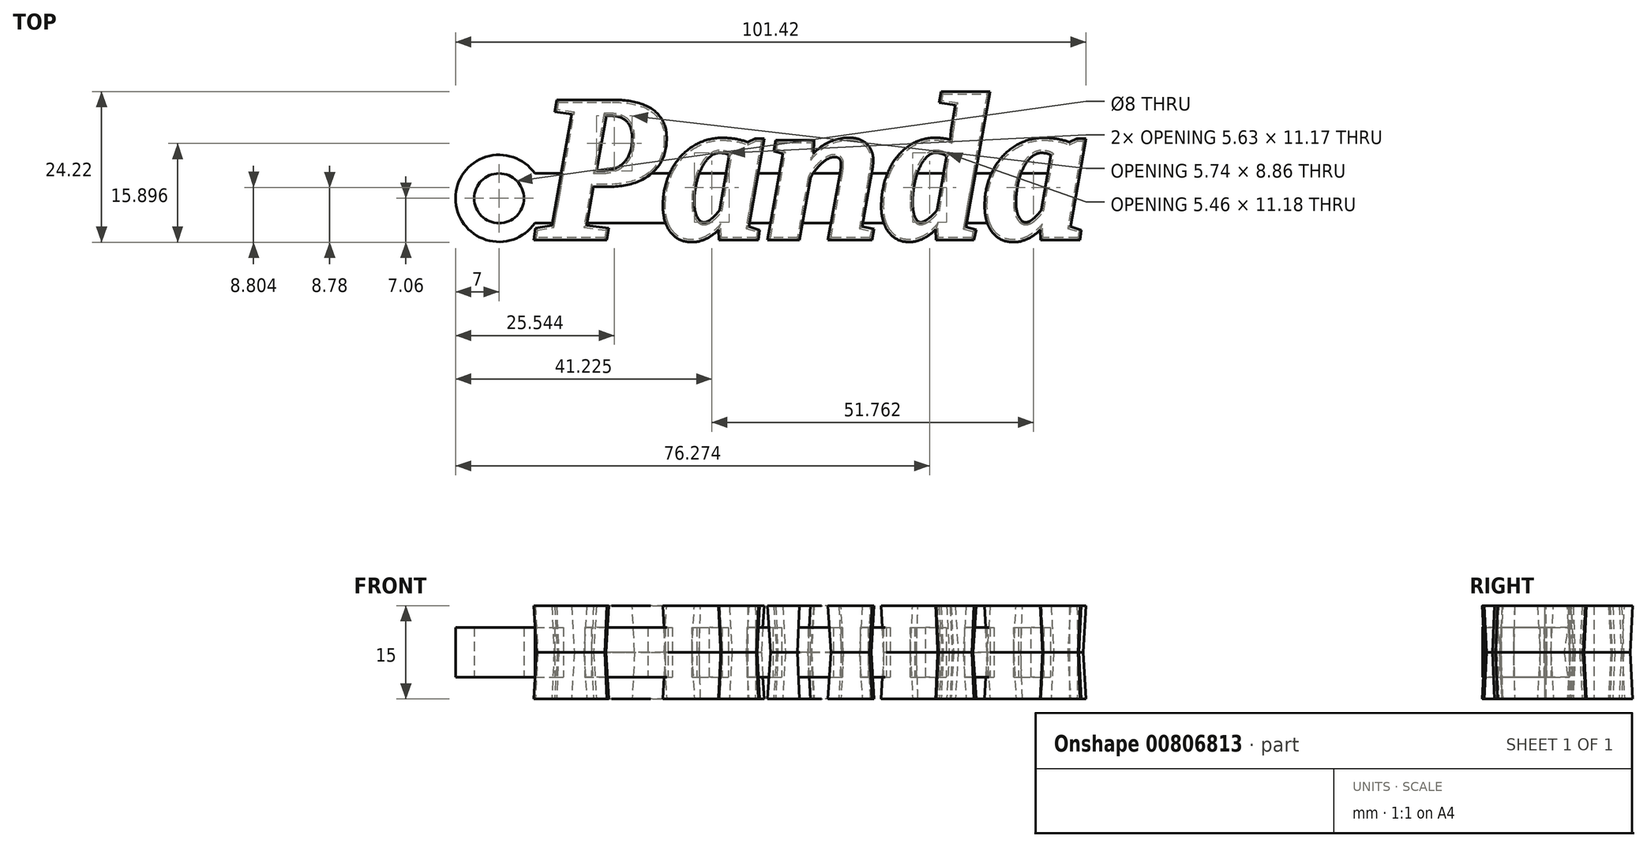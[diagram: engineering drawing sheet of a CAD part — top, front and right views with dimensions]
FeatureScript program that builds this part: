
annotation { "Feature Type Name" : "Feature", "Feature Type Description" : "" }
export const myFeature = defineFeature(function(context is Context, id is Id, definition is map)
    precondition{}
    {
        {
            var Q0;
            Q0=qCreatedBy(makeId("Top.planeOp"),FACE);
            var sketch = newSketch(context, id + "F0", { "sketchPlane" : qUnion([Q0])});
            skLineSegment(sketch, "E0.bottom", {"start": v(-45, 0) * mm, "end": v(45, 0) * mm});
            skLineSegment(sketch, "E0.top", {"start": v(-45, -8) * mm, "end": v(45, -8) * mm});
            skLineSegment(sketch, "E0.left", {"start": v(-45, 0) * mm, "end": v(-45, -8) * mm});
            skLineSegment(sketch, "E0.right", {"start": v(45, 0) * mm, "end": v(45, -8) * mm});
            skCircle(sketch, "E1", {"center": v(-45, -4) * mm, "radius": 7 * mm});
            skCircle(sketch, "E2.0", {"center": v(-45, -4) * mm, "radius": 4 * mm});
            skText(sketch, "E3", { "text": "Panda", "fontName": "Tinos-BoldItalic.ttf"});
            const initialGuessF0  = {"E3": [-0.03896, -0.01032, 1, 0, 0.02395]};
            skSetInitialGuess(sketch, initialGuessF0);
            skSolve(sketch);
        }
        {
            var Q0;
            {var subQ2=sQuery(id+"F0.wireOp",EDGE,"E0.bottom");var subQ4=sQuery(id+"F0.wireOp",EDGE,"E1");var subQ5=makeQuery(id+"F0.imprint","INTERSECT",VERTEX,{"derivedFrom":[subQ2,subQ4]});Q0=makeQuery(id+"F0.imprint","IMPRINT",FACE,{"disambiguationData":[TD([[makeQuery(id+"F0.imprint","IMPRINT",EDGE,{"disambiguationData":[TD([[subQ5,-1.0]])],"derivedFrom":subQ4}),1.0]])]});}
            var Q1;
            {var subQ2=sQuery(id+"F0.wireOp",EDGE,"E0.bottom");var subQ4=sQuery(id+"F0.wireOp",EDGE,"E1");var subQ5=makeQuery(id+"F0.imprint","INTERSECT",VERTEX,{"derivedFrom":[subQ2,subQ4]});Q1=makeQuery(id+"F0.imprint","IMPRINT",FACE,{"disambiguationData":[TD([[makeQuery(id+"F0.imprint","IMPRINT",EDGE,{"disambiguationData":[TD([[subQ5,1.0]])],"derivedFrom":subQ4}),1.0]])]});}
            var Q2;
            {var subQ0=sQuery(id+"F0.wireOp",EDGE,"E1");var subQ1=sQuery(id+"F0.wireOp",EDGE,"E0.bottom");var subQ2=makeQuery(id+"F0.imprint","INTERSECT",VERTEX,{"derivedFrom":[subQ1,subQ0]});Q2=makeQuery(id+"F0.imprint","IMPRINT",FACE,{"disambiguationData":[TD([[makeQuery(id+"F0.imprint","IMPRINT",EDGE,{"disambiguationData":[TD([[subQ2,-1.0]])],"derivedFrom":subQ1}),-1.0]])]});}
            var Q3;
            {var subQ0=sQuery(id+"F0.wireOp",EDGE,"E3.sketch_text.stroke-20");Q3=makeQuery(id+"F0.imprint","IMPRINT",FACE,{"disambiguationData":[TD([[makeQuery(id+"F0.imprint","IMPRINT",EDGE,{"derivedFrom":subQ0}),1.0]])]});}
            var Q4;
            {var subQ5=sQuery(id+"F0.wireOp",EDGE,"E3.sketch_text.stroke-45");Q4=makeQuery(id+"F0.imprint","IMPRINT",FACE,{"disambiguationData":[TD([[makeQuery(id+"F0.imprint","IMPRINT",EDGE,{"derivedFrom":subQ5}),1.0]])]});}
            var Q5;
            {var subQ0=sQuery(id+"F0.wireOp",EDGE,"E3.sketch_text.stroke-36");var subQ1=sQuery(id+"F0.wireOp",EDGE,"E0.bottom");var subQ2=makeQuery(id+"F0.imprint","INTERSECT",VERTEX,{"derivedFrom":[subQ1,subQ0]});Q5=makeQuery(id+"F0.imprint","IMPRINT",FACE,{"disambiguationData":[TD([[makeQuery(id+"F0.imprint","IMPRINT",EDGE,{"disambiguationData":[TD([[subQ2,-1.0]])],"derivedFrom":subQ1}),-1.0]])]});}
            var Q6;
            {var subQ5=sQuery(id+"F0.wireOp",EDGE,"E3.sketch_text.stroke-68");Q6=makeQuery(id+"F0.imprint","IMPRINT",FACE,{"disambiguationData":[TD([[makeQuery(id+"F0.imprint","IMPRINT",EDGE,{"derivedFrom":subQ5}),1.0]])]});}
            var Q7;
            {var subQ5=sQuery(id+"F0.wireOp",EDGE,"E3.sketch_text.stroke-94");Q7=makeQuery(id+"F0.imprint","IMPRINT",FACE,{"disambiguationData":[TD([[makeQuery(id+"F0.imprint","IMPRINT",EDGE,{"derivedFrom":subQ5}),1.0]])]});}
            var Q8;
            {var subQ0=sQuery(id+"F0.wireOp",EDGE,"E3.sketch_text.stroke-103");Q8=makeQuery(id+"F0.imprint","IMPRINT",FACE,{"disambiguationData":[TD([[makeQuery(id+"F0.imprint","IMPRINT",EDGE,{"derivedFrom":subQ0}),1.0]])]});}
            var Q9;
            {var subQ5=sQuery(id+"F0.wireOp",EDGE,"E3.sketch_text.stroke-118");Q9=makeQuery(id+"F0.imprint","IMPRINT",FACE,{"disambiguationData":[TD([[makeQuery(id+"F0.imprint","IMPRINT",EDGE,{"derivedFrom":subQ5}),1.0]])]});}
            var Q10;
            {var subQ1=sQuery(id+"F0.wireOp",EDGE,"E3.sketch_text.stroke-48");var subQ3=sQuery(id+"F0.wireOp",EDGE,"E0.bottom");var subQ4=makeQuery(id+"F0.imprint","INTERSECT",VERTEX,{"derivedFrom":[subQ3,subQ1]});Q10=makeQuery(id+"F0.imprint","IMPRINT",FACE,{"disambiguationData":[TD([[makeQuery(id+"F0.imprint","IMPRINT",EDGE,{"disambiguationData":[TD([[subQ4,-1.0]])],"derivedFrom":subQ3}),-1.0]])]});}
            extrude(context, id + "F1", {"entities" : qUnion([Q0, Q1, Q2, Q3, Q4, Q5, Q6, Q7, Q8, Q9, Q10]), "endBound" : BoundingType.SYMMETRIC, "depth" : 8 * mm, "offsetDistance" : 25 * mm});
        }
        {
            var Q0;
            Q0=makeQuery(id+"F0.imprint","IMPRINT",FACE,{"disambiguationData":[TD([[makeQuery(id+"F0.imprint","IMPRINT",EDGE,{"derivedFrom":sQuery(id+"F0.wireOp",EDGE,"E3.sketch_text.stroke-0")}),-1.0]])]});
            var Q1;
            {var subQ0=sQuery(id+"F0.wireOp",EDGE,"E3.sketch_text.stroke-21");Q1=makeQuery(id+"F0.imprint","IMPRINT",FACE,{"disambiguationData":[TD([[makeQuery(id+"F0.imprint","IMPRINT",EDGE,{"derivedFrom":subQ0}),-1.0]])]});}
            var Q2;
            {var subQ0=sQuery(id+"F0.wireOp",EDGE,"E3.sketch_text.stroke-8");Q2=makeQuery(id+"F0.imprint","IMPRINT",FACE,{"disambiguationData":[TD([[makeQuery(id+"F0.imprint","IMPRINT",EDGE,{"derivedFrom":subQ0}),-1.0]])]});}
            var Q3;
            {var subQ8=sQuery(id+"F0.wireOp",EDGE,"E3.sketch_text.stroke-37");Q3=makeQuery(id+"F0.imprint","IMPRINT",FACE,{"disambiguationData":[TD([[makeQuery(id+"F0.imprint","IMPRINT",EDGE,{"derivedFrom":subQ8}),-1.0]])]});}
            var Q4;
            {var subQ5=sQuery(id+"F0.wireOp",EDGE,"E3.sketch_text.stroke-40");Q4=makeQuery(id+"F0.imprint","IMPRINT",FACE,{"disambiguationData":[TD([[makeQuery(id+"F0.imprint","IMPRINT",EDGE,{"derivedFrom":subQ5}),-1.0]])]});}
            var Q5;
            {var subQ11=sQuery(id+"F0.wireOp",EDGE,"E3.sketch_text.stroke-31");Q5=makeQuery(id+"F0.imprint","IMPRINT",FACE,{"disambiguationData":[TD([[makeQuery(id+"F0.imprint","IMPRINT",EDGE,{"derivedFrom":subQ11}),-1.0]])]});}
            var Q6;
            {var subQ11=sQuery(id+"F0.wireOp",EDGE,"E3.sketch_text.stroke-22");Q6=makeQuery(id+"F0.imprint","IMPRINT",FACE,{"disambiguationData":[TD([[makeQuery(id+"F0.imprint","IMPRINT",EDGE,{"derivedFrom":subQ11}),-1.0]])]});}
            var Q7;
            {var subQ3=sQuery(id+"F0.wireOp",EDGE,"E0.bottom");var subQ5=sQuery(id+"F0.wireOp",EDGE,"E3.sketch_text.stroke-51");var subQ6=makeQuery(id+"F0.imprint","INTERSECT",VERTEX,{"derivedFrom":[subQ3,subQ5]});Q7=makeQuery(id+"F0.imprint","IMPRINT",FACE,{"disambiguationData":[TD([[makeQuery(id+"F0.imprint","IMPRINT",EDGE,{"disambiguationData":[TD([[subQ6,-1.0]])],"derivedFrom":subQ3}),-1.0]])]});}
            var Q8;
            {var subQ11=sQuery(id+"F0.wireOp",EDGE,"E3.sketch_text.stroke-46");Q8=makeQuery(id+"F0.imprint","IMPRINT",FACE,{"disambiguationData":[TD([[makeQuery(id+"F0.imprint","IMPRINT",EDGE,{"derivedFrom":subQ11}),-1.0]])]});}
            var Q9;
            {var subQ1=sQuery(id+"F0.wireOp",EDGE,"E3.sketch_text.stroke-59");var subQ5=sQuery(id+"F0.wireOp",EDGE,"E0.bottom");var subQ6=makeQuery(id+"F0.imprint","INTERSECT",VERTEX,{"derivedFrom":[subQ5,subQ1]});Q9=makeQuery(id+"F0.imprint","IMPRINT",FACE,{"disambiguationData":[TD([[makeQuery(id+"F0.imprint","IMPRINT",EDGE,{"disambiguationData":[TD([[subQ6,1.0]])],"derivedFrom":subQ5}),-1.0]])]});}
            var Q10;
            {var subQ0=sQuery(id+"F0.wireOp",EDGE,"E3.sketch_text.stroke-61");Q10=makeQuery(id+"F0.imprint","IMPRINT",FACE,{"disambiguationData":[TD([[makeQuery(id+"F0.imprint","IMPRINT",EDGE,{"derivedFrom":subQ0}),-1.0]])]});}
            var Q11;
            {var subQ5=sQuery(id+"F0.wireOp",EDGE,"E3.sketch_text.stroke-50");Q11=makeQuery(id+"F0.imprint","IMPRINT",FACE,{"disambiguationData":[TD([[makeQuery(id+"F0.imprint","IMPRINT",EDGE,{"derivedFrom":subQ5}),-1.0]])]});}
            var Q12;
            {var subQ5=sQuery(id+"F0.wireOp",EDGE,"E3.sketch_text.stroke-85");Q12=makeQuery(id+"F0.imprint","IMPRINT",FACE,{"disambiguationData":[TD([[makeQuery(id+"F0.imprint","IMPRINT",EDGE,{"derivedFrom":subQ5}),-1.0]])]});}
            var Q13;
            {var subQ14=sQuery(id+"F0.wireOp",EDGE,"E3.sketch_text.stroke-88");Q13=makeQuery(id+"F0.imprint","IMPRINT",FACE,{"disambiguationData":[TD([[makeQuery(id+"F0.imprint","IMPRINT",EDGE,{"derivedFrom":subQ14}),-1.0]])]});}
            var Q14;
            {var subQ8=sQuery(id+"F0.wireOp",EDGE,"E3.sketch_text.stroke-69");Q14=makeQuery(id+"F0.imprint","IMPRINT",FACE,{"disambiguationData":[TD([[makeQuery(id+"F0.imprint","IMPRINT",EDGE,{"derivedFrom":subQ8}),-1.0]])]});}
            var Q15;
            {var subQ0=sQuery(id+"F0.wireOp",EDGE,"E3.sketch_text.stroke-79");Q15=makeQuery(id+"F0.imprint","IMPRINT",FACE,{"disambiguationData":[TD([[makeQuery(id+"F0.imprint","IMPRINT",EDGE,{"derivedFrom":subQ0}),-1.0]])]});}
            var Q16;
            {var subQ0=sQuery(id+"F0.wireOp",EDGE,"E3.sketch_text.stroke-66");Q16=makeQuery(id+"F0.imprint","IMPRINT",FACE,{"disambiguationData":[TD([[makeQuery(id+"F0.imprint","IMPRINT",EDGE,{"derivedFrom":subQ0}),-1.0]])]});}
            var Q17;
            {var subQ11=sQuery(id+"F0.wireOp",EDGE,"E3.sketch_text.stroke-110");Q17=makeQuery(id+"F0.imprint","IMPRINT",FACE,{"disambiguationData":[TD([[makeQuery(id+"F0.imprint","IMPRINT",EDGE,{"derivedFrom":subQ11}),-1.0]])]});}
            var Q18;
            {var subQ7=sQuery(id+"F0.wireOp",EDGE,"E0.right");Q18=makeQuery(id+"F0.imprint","IMPRINT",FACE,{"disambiguationData":[TD([[makeQuery(id+"F0.imprint","IMPRINT",EDGE,{"derivedFrom":subQ7}),1.0]])]});}
            var Q19;
            {var subQ4=sQuery(id+"F0.wireOp",EDGE,"E0.right");Q19=makeQuery(id+"F0.imprint","IMPRINT",FACE,{"disambiguationData":[TD([[makeQuery(id+"F0.imprint","IMPRINT",EDGE,{"derivedFrom":subQ4}),-1.0]])]});}
            extrude(context, id + "F2", {"entities" : qUnion([Q0, Q1, Q2, Q3, Q4, Q5, Q6, Q7, Q8, Q9, Q10, Q11, Q12, Q13, Q14, Q15, Q16, Q17, Q18, Q19]), "endBound" : BoundingType.SYMMETRIC, "depth" : 15 * mm, "offsetDistance" : 25 * mm, "hasDraft" : true, "draftAngle" : 3 * degree});
        }
    });
